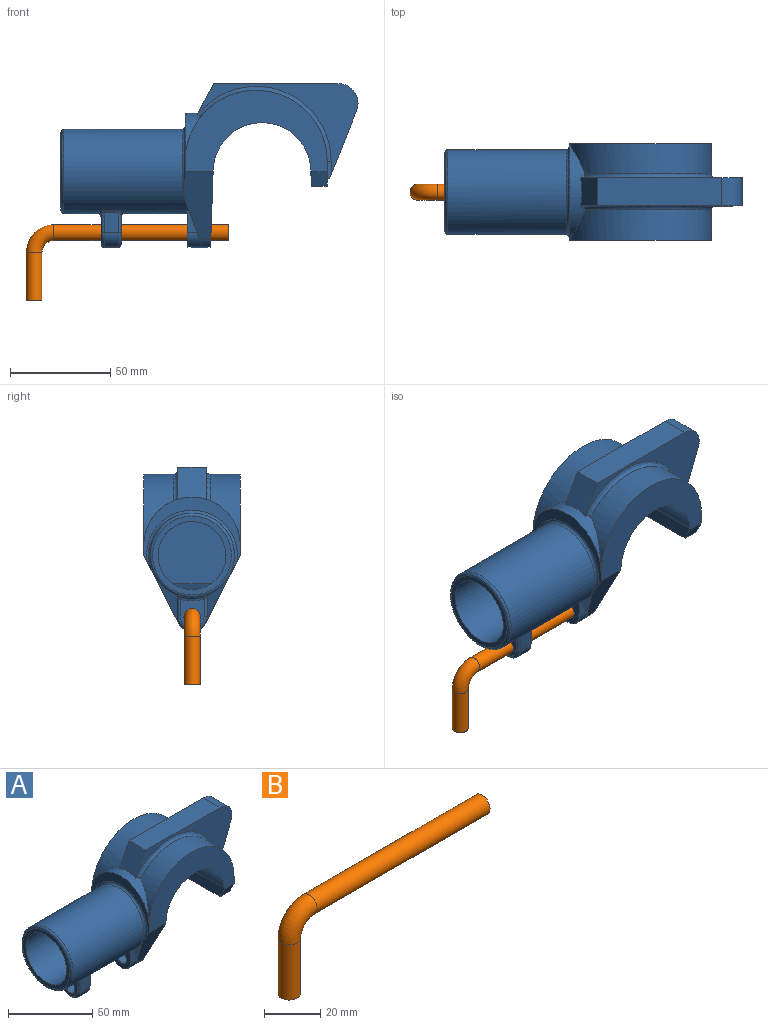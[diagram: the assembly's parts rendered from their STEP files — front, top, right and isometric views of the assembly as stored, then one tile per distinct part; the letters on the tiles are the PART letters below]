
ASSEMBLY  parts=2 mates=1
PART A: 63 faces, bbox 148.7x49.3x86 mm
  f0: cylinder r=21.2mm len=62.62mm, axis (1,0,0), area 7740.6mm2, adj f1,f2,f41,f43,f44,f46,f47,f49
  f1: plane 24.1x12.21mm, normal (-0.94,0,-0.34), area 61.4mm2, adj f0,f15,f54,f58,f60
  f2: plane 28.33x18.79mm, normal (-0.94,0,-0.34), area 63.1mm2, adj f0,f14,f16,f54,f59,f60
  f3: cylinder r=35.53mm len=71.06mm, axis (0,1,0), area 1428.5mm2, adj f5,f12,f27,f29
  f4: cylinder r=35.53mm len=71.06mm, axis (0,1,0), area 1428.5mm2, adj f5,f10,f25,f29
  f5: plane 48.2x12.36mm, normal (1,0,0), area 413.2mm2, adj f3,f4,f9,f10,f12,f13,f17,f18
  f6: plane 48.2x32.34mm, normal (-1,0,0), area 350.6mm2, adj f10,f12,f14,f15,f29,f54
  f7: plane 48.2x38.85mm, normal (1,0,-0.03), area 1125.1mm2, adj f10,f11,f12,f14,f15,f16
  f8: plane 48.2x8.16mm, normal (-1,0,-0.03), area 366.3mm2, adj f9,f10,f11,f12,f13,f17
  f9: plane 40.72x7.92mm, normal (0,0,-1), area 322.5mm2, adj f5,f8,f13,f17
  f10: plane 71.06x40.61mm, normal (0,1,0), area 1407.3mm2, adj f4,f5,f6,f7,f8,f11,f13,f14
  f11: cylinder r=24.4mm len=48.77mm, axis (0,1,0), area 3612.7mm2, adj f7,f8,f10,f12
  f12: plane 71.06x40.61mm, normal (0,-1,0), area 1407.3mm2, adj f3,f5,f6,f7,f8,f11,f15,f17
  f13: plane 8.17x7.28mm, normal (0,0.89,-0.46), area 65.8mm2, adj f5,f8,f9,f10
  f14: plane 33.9x17.43mm, normal (0,0.89,-0.46), area 436.6mm2, adj f2,f6,f7,f10,f16,f54
  f15: plane 33.9x17.43mm, normal (0,-0.89,-0.46), area 436.6mm2, adj f1,f6,f7,f12,f16,f54,f56
  f16: cylinder r=7.5mm len=13.34mm, axis (1,0,0), area 75mm2, adj f2,f7,f14,f15,f56
  f17: plane 8.17x7.28mm, normal (0,-0.89,-0.46), area 65.8mm2, adj f5,f8,f9,f12
  f18: plane 18x1.21mm, normal (0,0,-1), area 18.6mm2, adj f5,f19,f26,f28
  f19: plane 33.92x14.37mm, normal (0.93,0,-0.37), area 510.7mm2, adj f18,f20,f23,f24,f26,f28
  f20: cylinder r=10mm len=14mm, axis (0,1,0), area 273mm2, adj f19,f21,f23,f24
  f21: plane 62x14mm, normal (0,0,1), area 868mm2, adj f20,f22,f23,f24
  f22: plane 15.89x14mm, normal (-0.88,0,0.48), area 242.4mm2, adj f21,f23,f24,f29
  f23: plane 80.68x45.59mm, normal (0,-1,0), area 824.3mm2, adj f19,f20,f21,f22,f27,f28,f29
  f24: plane 80.68x45.59mm, normal (0,1,0), area 824.3mm2, adj f19,f20,f21,f22,f25,f26,f29
  f25: torus R=37.53mm, axis (0,-1,0), area 280.3mm2, adj f4,f24,f26,f29
  f26: cylinder r=2mm len=8.62mm, axis (0,0,-1), area 26.3mm2, adj f5,f18,f19,f24,f25
  f27: torus R=37.53mm, axis (0,-1,0), area 280.3mm2, adj f3,f23,f28,f29
  f28: cylinder r=2mm len=8.62mm, axis (0,0,1), area 26.3mm2, adj f5,f18,f19,f23,f27
  f29: cylinder r=24.1mm len=48.2mm, axis (-1,0,0), area 298.9mm2, adj f3,f4,f6,f22,f23,f24,f25,f27
  f30: cylinder r=17mm len=63.09mm, axis (1,0,0), area 6637.3mm2, adj f31,f32,f33
  f31: plane 39.4x39.4mm, normal (-1,0,0), area 311.3mm2, adj f30,f55
  f32: plane 19.29x3mm, normal (-0.94,0,-0.34), area 41.8mm2, adj f30,f33
  f33: plane 34x31mm, normal (-1,0,0), area 868.6mm2, adj f30,f32
  f34: plane 9.13x7mm, normal (0,1,0), area 63.9mm2, adj f35,f45,f50,f53
  f35: cylinder r=7.5mm len=15mm, axis (1,0,0), area 167.4mm2, adj f34,f37,f42,f51
  f36: cylinder r=4.05mm len=10mm, axis (1,0,0), area 254.5mm2, adj f38,f39
  f37: plane 9.97x7mm, normal (0,-1,-0.02), area 69.8mm2, adj f35,f40,f43,f48
  f38: plane 14.66x12.2mm, normal (-1,0,0), area 102.6mm2, adj f36,f40,f42,f44,f45
  f39: plane 14.66x12.2mm, normal (1,0,0), area 102.6mm2, adj f36,f48,f49,f51,f53
  f40: cylinder r=1.5mm len=10.01mm, axis (0,0.02,-1), area 22.4mm2, adj f37,f38,f41,f42
  f41: bspline ~3.18x2.99mm, area 6.8mm2, adj f0,f40,f43,f44
  f42: torus R=6mm, axis (-1,0,0), area 52.3mm2, adj f35,f38,f40,f45
  f43: cylinder r=1.5mm len=7mm, axis (1,0,0), area 11.9mm2, adj f0,f37,f41,f46
  f44: torus R=22.7mm, axis (-1,0,0), area 27.8mm2, adj f0,f38,f41,f47
  f45: cylinder r=1.5mm len=9.19mm, axis (0,0,1), area 20.6mm2, adj f34,f38,f42,f47
  f46: bspline ~3.62x3.18mm, area 6.8mm2, adj f0,f43,f48,f49
  f47: bspline ~3.62x3.17mm, area 6.8mm2, adj f0,f44,f45,f50
  f48: cylinder r=1.5mm len=10.01mm, axis (0,-0.02,1), area 22.4mm2, adj f37,f39,f46,f51
  f49: torus R=22.7mm, axis (-1,0,0), area 27.8mm2, adj f0,f39,f46,f52
  f50: cylinder r=1.5mm len=7mm, axis (1,0,0), area 12.2mm2, adj f0,f34,f47,f52
  f51: torus R=6mm, axis (-1,0,0), area 52.3mm2, adj f35,f39,f48,f53
  f52: bspline ~3.62x3.44mm, area 6.8mm2, adj f0,f49,f50,f53
  f53: cylinder r=1.5mm len=9.19mm, axis (0,0,-1), area 20.6mm2, adj f34,f39,f51,f52
  f54: torus R=22.7mm, axis (1,0,0), area 198.7mm2, adj f0,f1,f2,f6,f14,f15
  f55: torus R=19.7mm, axis (-1,0,0), area 305.8mm2, adj f0,f31
  f56: plane 6.93x4.23mm, normal (0.94,0,0.34), area 0mm2, adj f15,f16,f60
  f57: plane 18.27x15.25mm, normal (-1,0,0), area 184.3mm2, adj f0,f58,f59,f60,f61
  f58: plane 10.94x5.06mm, normal (0,-1,-0.02), area 33.6mm2, adj f0,f1,f57,f60
  f59: plane 10.14x4.81mm, normal (0,1,0), area 30.1mm2, adj f0,f2,f57,f60
  f60: cylinder r=7.5mm len=15mm, axis (-1,0,0), area 160.4mm2, adj f1,f2,f56,f57,f58,f59
  f61: cylinder r=4.05mm len=8.1mm, axis (-1,0,0), area 127.2mm2, adj f57,f62
  f62: plane 8.1x8.1mm, normal (-0.94,0,-0.34), area 54.8mm2, adj f61
PART B: 5 faces, bbox 102.2x8x39.2 mm
  f0: plane 8x8mm, normal (0,0,-1), area 50.3mm2, adj f2
  f1: plane 8x8mm, normal (1,0,0), area 50.3mm2, adj f4
  f2: cylinder r=4mm len=24mm, axis (0,0,1), area 603.2mm2, adj f0,f3
  f3: torus R=10mm, axis (0,1,0), area 394.8mm2, adj f2,f4
  f4: cylinder r=4mm len=87mm, axis (1,0,0), area 2186.5mm2, adj f1,f3
PLACE A t=(-9.99,-60.69,21.55)mm
PLACE B t=(-123.96,-60.69,-42.95)mm
MATE fastened A.f60 <-> B.f4  axis (-1,0,0) through (-90.46,-60.69,-8.95)mm
